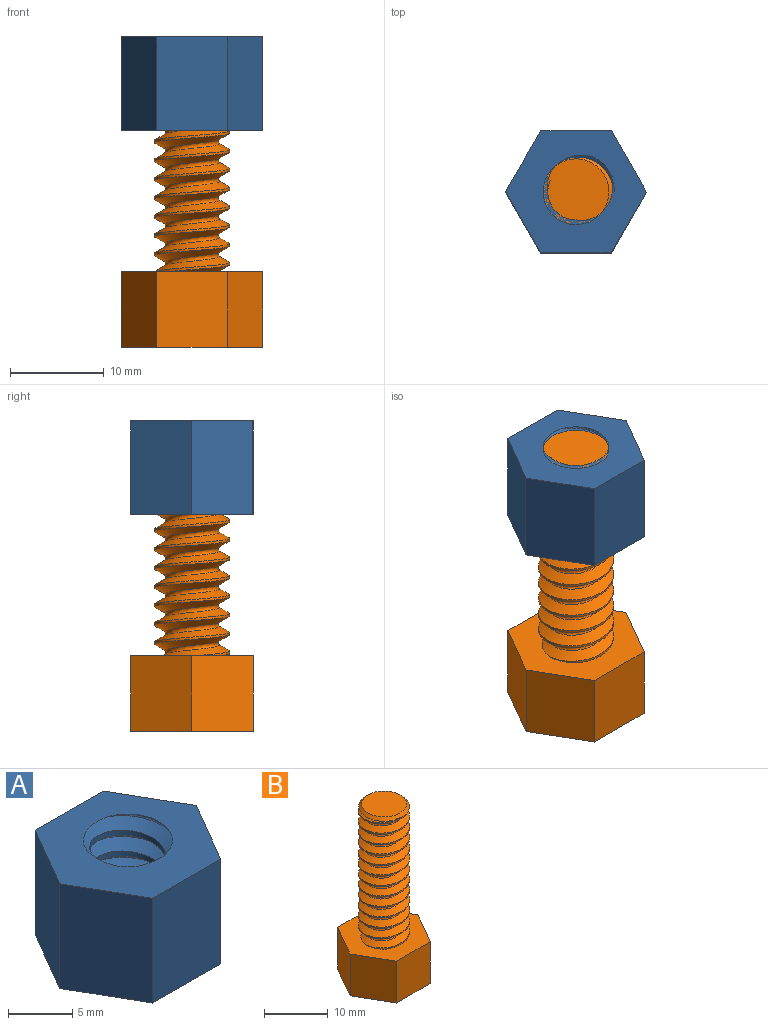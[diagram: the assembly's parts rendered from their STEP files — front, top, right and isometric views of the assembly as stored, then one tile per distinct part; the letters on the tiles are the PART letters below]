
ASSEMBLY  parts=2 mates=1
PART A: 12 faces, bbox 15.1x13.1x11.7 mm
  f0: plane 10x7.51mm, normal (0,-1,0), area 75.1mm2, adj f1,f5,f6,f7
  f1: plane 10x6.49mm, normal (0.86,-0.5,0), area 75.1mm2, adj f0,f2,f6,f7
  f2: plane 10x6.51mm, normal (0.87,0.5,0), area 75.1mm2, adj f1,f3,f6,f7
  f3: plane 10x7.51mm, normal (0,1,0), area 75.1mm2, adj f2,f4,f6,f7
  f4: plane 10x6.49mm, normal (-0.86,0.5,0), area 75.1mm2, adj f3,f5,f6,f7
  f5: plane 10x6.51mm, normal (-0.87,-0.5,0), area 75.1mm2, adj f0,f4,f6,f7
  f6: plane 15.08x13.1mm, normal (0,0,1), area 107.8mm2, adj f0,f1,f2,f3,f4,f5,f8,f9
  f7: plane 15.08x13.1mm, normal (0,0,-1), area 107.8mm2, adj f0,f1,f2,f3,f4,f5,f8,f9
  f8: bspline ~11.29x9.43mm, area 139.4mm2, adj f6,f7,f10,f11
  f9: bspline ~11.63x9.43mm, area 139.5mm2, adj f6,f7,f10,f11
  f10: bspline ~10.92x9.64mm, area 37.6mm2, adj f6,f7,f8,f9
  f11: cylinder r=3mm len=10mm, axis (0,0,1), area 45.7mm2, adj f6,f7,f8,f9
PART B: 15 faces, bbox 15.6x13.6x34 mm
  f0: plane 8x7.51mm, normal (0,-1,0), area 60mm2, adj f1,f5,f6,f7
  f1: plane 8x6.5mm, normal (0.87,-0.5,0), area 60mm2, adj f0,f2,f6,f7
  f2: plane 8x6.5mm, normal (0.87,0.5,0), area 60mm2, adj f1,f3,f6,f7
  f3: plane 8x7.51mm, normal (0,1,0), area 60mm2, adj f2,f4,f6,f7
  f4: plane 8x6.5mm, normal (-0.87,0.5,0), area 60mm2, adj f3,f5,f6,f7
  f5: plane 8x6.5mm, normal (-0.87,-0.5,0), area 60mm2, adj f0,f4,f6,f7
  f6: plane 15.55x13.54mm, normal (0,0,1), area 110mm2, adj f0,f1,f2,f3,f4,f5,f8,f11
  f7: plane 15.01x13mm, normal (0,0,-1), area 146.4mm2, adj f0,f1,f2,f3,f4,f5
  f8: cylinder r=4mm len=24.5mm, axis (0,0,-1), area 91.7mm2, adj f6,f10,f12,f13
  f9: plane 7x7mm, normal (0,0,1), area 38.5mm2, adj f10
  f10: cone r=3.5mm half-angle=45deg, axis (0,0,-1), area 16.7mm2, adj f8,f9,f14
  f11: bspline ~25.83x6.74mm, area 122.9mm2, adj f6,f12,f13,f14
  f12: bspline ~26.29x9.24mm, area 334.2mm2, adj f6,f8,f11,f14
  f13: bspline ~25.96x9.24mm, area 333.5mm2, adj f6,f8,f11,f14
  f14: plane 8.55x8.55mm, normal (0,0,-1), area 14mm2, adj f10,f11,f12,f13
PLACE A t=(0.74,-25.73,10.39)mm
PLACE B t=(0.74,-25.73,-12.61)mm
MATE fastened A.f11 <-> B.f8  axis (0,0,1) through (0.74,-25.73,20.39)mm
